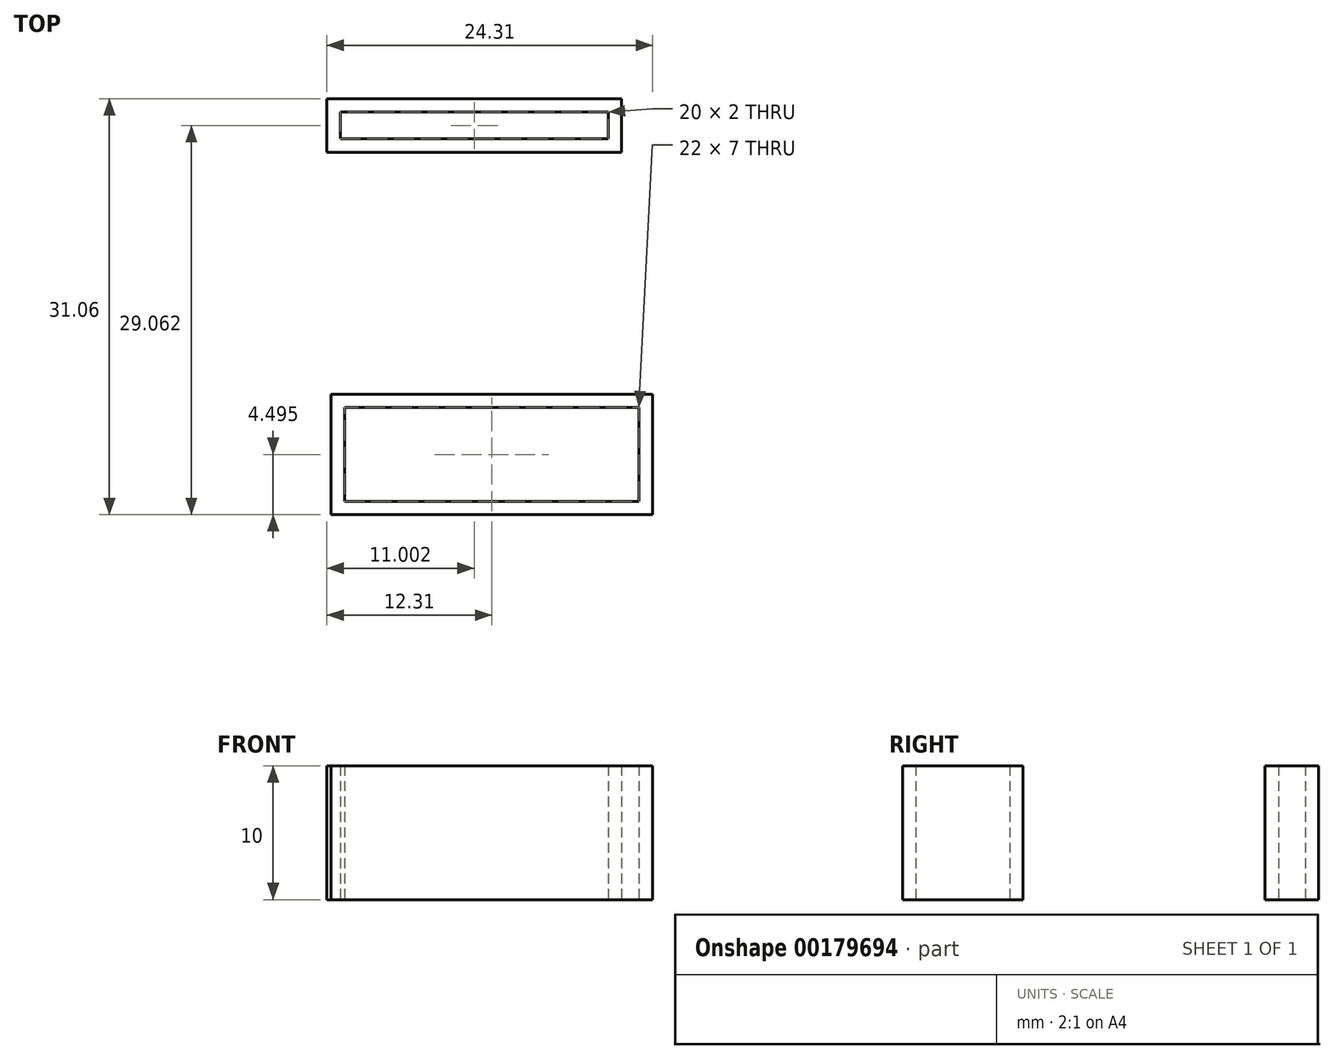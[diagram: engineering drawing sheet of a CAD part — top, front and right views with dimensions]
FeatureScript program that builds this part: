
annotation { "Feature Type Name" : "Feature", "Feature Type Description" : "" }
export const myFeature = defineFeature(function(context is Context, id is Id, definition is map)
    precondition{}
    {
        {
            var Q0;
            Q0=qCreatedBy(makeId("Top.planeOp"),FACE);
            var sketch = newSketch(context, id + "F0", { "sketchPlane" : qUnion([Q0])});
            skLineSegment(sketch, "E0.bottom", {"start": v(-44.09, 17) * mm, "end": v(-24.09, 17) * mm});
            skLineSegment(sketch, "E0.top", {"start": v(-44.09, 15) * mm, "end": v(-24.09, 15) * mm});
            skLineSegment(sketch, "E0.left", {"start": v(-44.09, 17) * mm, "end": v(-44.09, 15) * mm});
            skLineSegment(sketch, "E0.right", {"start": v(-24.09, 17) * mm, "end": v(-24.09, 15) * mm});
            skLineSegment(sketch, "E1.0", {"start": v(-45.09, 14) * mm, "end": v(-23.09, 14) * mm});
            skLineSegment(sketch, "E1.1", {"start": v(-45.09, 18) * mm, "end": v(-45.09, 14) * mm});
            skLineSegment(sketch, "E1.2", {"start": v(-45.09, 18) * mm, "end": v(-23.09, 18) * mm});
            skLineSegment(sketch, "E1.3", {"start": v(-23.09, 18) * mm, "end": v(-23.09, 14) * mm});
            skLineSegment(sketch, "E2.bottom", {"start": v(-43.78, -5.07) * mm, "end": v(-21.78, -5.07) * mm});
            skLineSegment(sketch, "E2.top", {"start": v(-43.78, -12.07) * mm, "end": v(-21.78, -12.07) * mm});
            skLineSegment(sketch, "E2.left", {"start": v(-43.78, -5.07) * mm, "end": v(-43.78, -12.07) * mm});
            skLineSegment(sketch, "E2.right", {"start": v(-21.78, -5.07) * mm, "end": v(-21.78, -12.07) * mm});
            skLineSegment(sketch, "E3.0", {"start": v(-44.78, -4.07) * mm, "end": v(-20.78, -4.07) * mm});
            skLineSegment(sketch, "E3.1", {"start": v(-44.78, -4.07) * mm, "end": v(-44.78, -13.07) * mm});
            skLineSegment(sketch, "E3.2", {"start": v(-44.78, -13.07) * mm, "end": v(-20.78, -13.07) * mm});
            skLineSegment(sketch, "E3.3", {"start": v(-20.78, -4.07) * mm, "end": v(-20.78, -13.07) * mm});
            skSolve(sketch);
        }
        {
            var Q0;
            Q0=makeQuery(id+"F0.imprint","IMPRINT",FACE,{"disambiguationData":[TD([[makeQuery(id+"F0.imprint","IMPRINT",EDGE,{"derivedFrom":sQuery(id+"F0.wireOp",EDGE,"E0.bottom")}),1.0]])]});
            var Q1;
            Q1=makeQuery(id+"F0.imprint","IMPRINT",FACE,{"disambiguationData":[TD([[makeQuery(id+"F0.imprint","IMPRINT",EDGE,{"derivedFrom":sQuery(id+"F0.wireOp",EDGE,"E2.bottom")}),1.0]])]});
            extrude(context, id + "F1", {"entities" : qUnion([Q0, Q1]), "depth" : 10 * mm, "offsetDistance" : 25 * mm});
        }
    });
